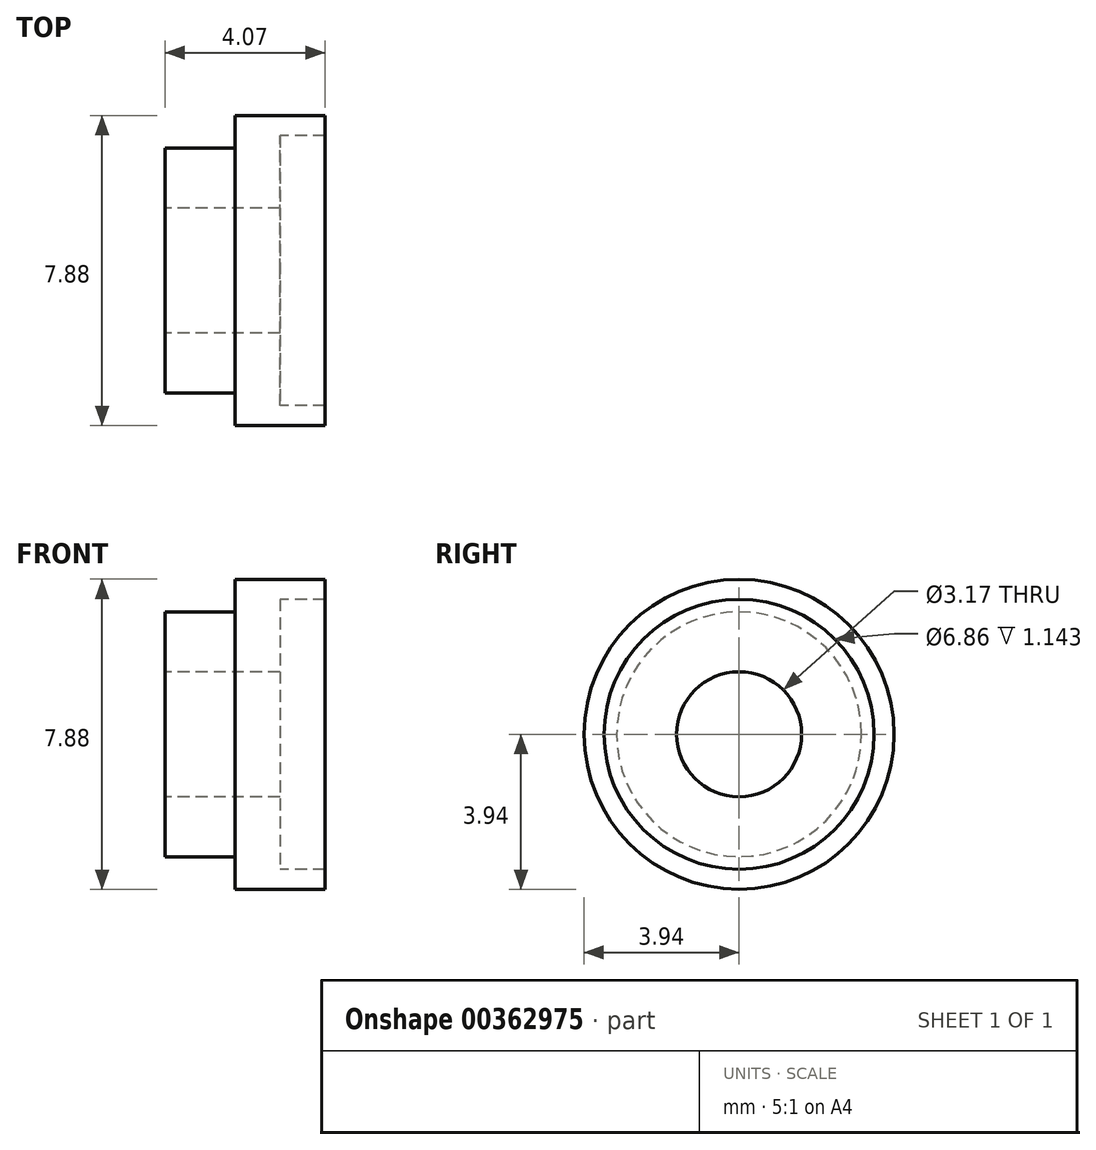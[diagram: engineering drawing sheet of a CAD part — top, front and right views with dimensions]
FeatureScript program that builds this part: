
annotation { "Feature Type Name" : "Feature", "Feature Type Description" : "" }
export const myFeature = defineFeature(function(context is Context, id is Id, definition is map)
    precondition{}
    {
        {
            var Q0;
            Q0=qCreatedBy(makeId("Front.planeOp"),FACE);
            var sketch = newSketch(context, id + "F0", { "sketchPlane" : qUnion([Q0])});
            skLineSegment(sketch, "E0", {"start": v(-2.06, 0) * mm, "end": v(3.82, 0) * mm});
            skLineSegment(sketch, "E1", {"start": v(-1.94, 1.59) * mm, "end": v(0.98, 1.59) * mm});
            skLineSegment(sketch, "E2", {"start": v(0.98, 1.59) * mm, "end": v(0.98, 3.43) * mm});
            skLineSegment(sketch, "E3", {"start": v(0.98, 3.43) * mm, "end": v(2.13, 3.43) * mm});
            skLineSegment(sketch, "E4", {"start": v(2.13, 3.43) * mm, "end": v(2.13, 3.94) * mm});
            skLineSegment(sketch, "E5", {"start": v(2.13, 3.94) * mm, "end": v(-0.16, 3.94) * mm});
            skLineSegment(sketch, "E6", {"start": v(-0.16, 3.94) * mm, "end": v(-0.16, 3.11) * mm});
            skLineSegment(sketch, "E7", {"start": v(-0.16, 3.11) * mm, "end": v(-1.94, 3.11) * mm});
            skLineSegment(sketch, "E8", {"start": v(-1.94, 3.11) * mm, "end": v(-1.94, 1.59) * mm});
            skSolve(sketch);
        }
        {
            var Q0;
            Q0=makeQuery(id+"F0.imprint","IMPRINT",FACE,{"disambiguationData":[TD([[makeQuery(id+"F0.imprint","IMPRINT",EDGE,{"derivedFrom":sQuery(id+"F0.wireOp",EDGE,"E1")}),1.0]])]});
            var Q1;
            Q1=sQuery(id+"F0.wireOp",EDGE,"E0");
            revolve(context, id + "F1", {"entities" : qUnion([Q0]), "axis" : qUnion([Q1]), "revolveType" : RevolveType.FULL});
        }
    });
